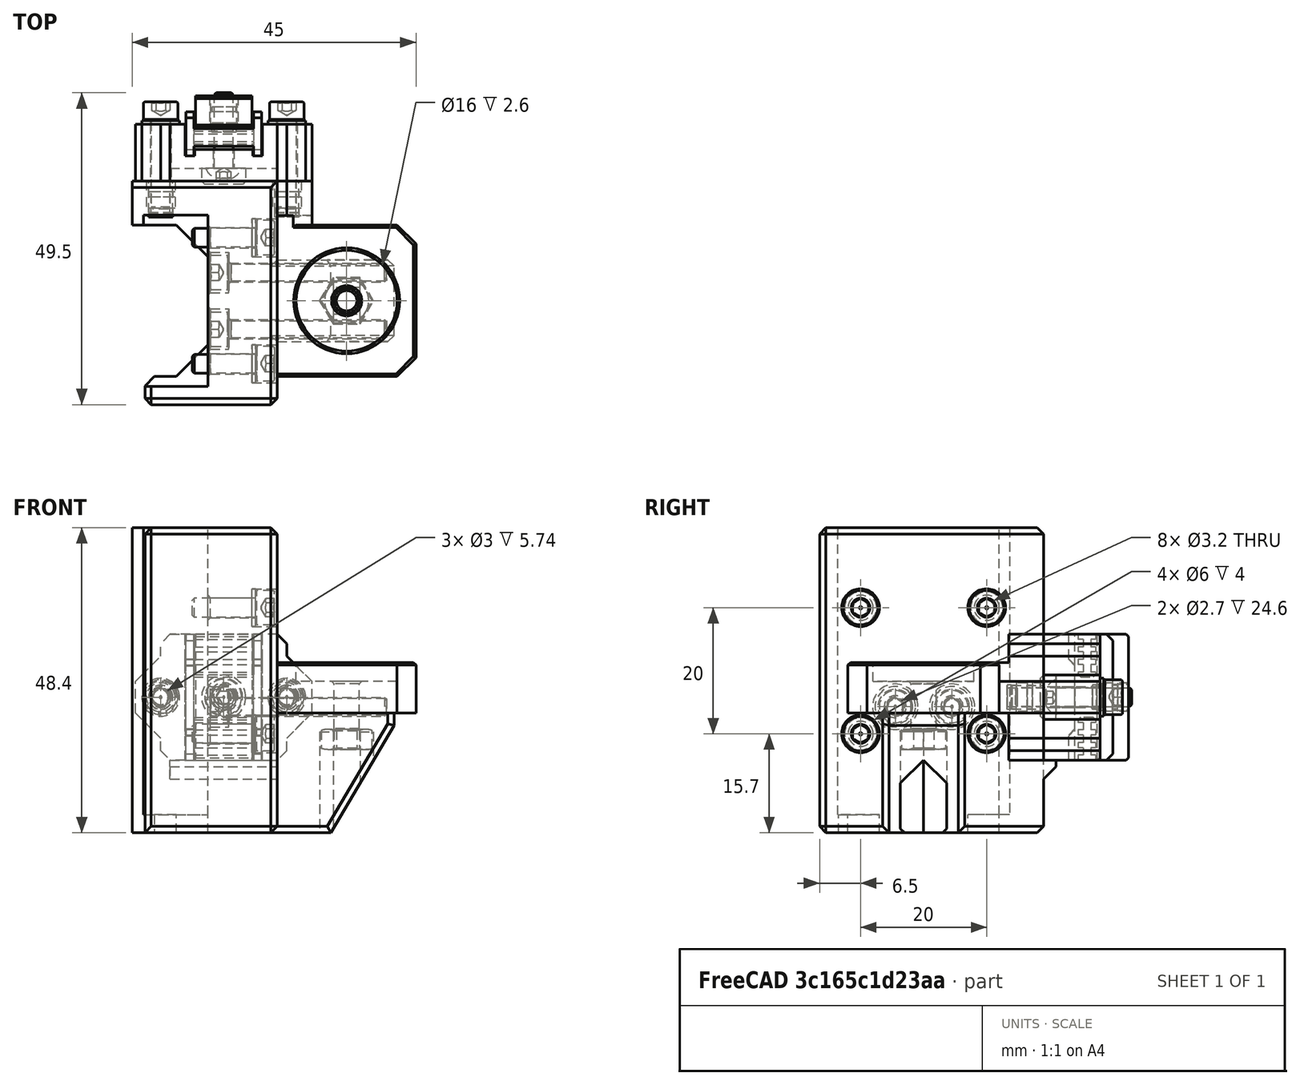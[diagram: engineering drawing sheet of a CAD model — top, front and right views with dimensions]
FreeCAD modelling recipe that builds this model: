
FCSTD DOCUMENT  (FreeCAD 0.19R24291 (Git))
Label: z-block-mount-left-assembly
License: Other
LicenseURL: GPL3
objects: Part::FeaturePython×19, Part::Feature×4, PartDesign::CoordinateSystem×1, App::Part×1
note: 24 computed .brp shape members not serialized (recipe doc carries the construction recipe); baked Part::Feature solids carry a one-line shape summary decoded from their .brp

FEATURE [Part::Feature] Cut002001001  label="z-belt-mounter-clamp-nut"
  Placement = pos=(2.5,36,18.5) rot=(-1,0,0;1.5708rad)
  shape: bbox 9 x 5 x 20 mm, 11 faces (baked)
FEATURE [Part::Feature] Chamfer004013007011015006002001  label="z-belt-block-mount"
  Placement = pos=(0,-12.5,0) rot=(0,0,1;0rad)
  shape: bbox 28 x 9 x 20 mm, 47 faces (baked)
FEATURE [Part::Feature] Cut028006004005011004003001010002002004006  label="z-belt-mounter-middle"
  Placement = pos=(0,-14,0) rot=(0,0,1;0rad)
  shape: bbox 12 x 7 x 20 mm, 80 faces (baked)
FEATURE [Part::FeaturePython] Washer  label="M3-Washer"  # Fasteners workbench fastener (typed FeaturePython)
  Placement = pos=(7,-10,32.7) rot=(0,1,0;1.5708rad)
  diameter = 4
  invert = false
  leftHanded = false
  matchOuter = true
  offset = 0
  type = 5
FEATURE [Part::FeaturePython] Washer001  label="M3-Washer008"  # Fasteners workbench fastener (typed FeaturePython)
  Placement = pos=(7,10,32.7) rot=(0,1,0;1.5708rad)
  diameter = 4
  invert = false
  leftHanded = false
  matchOuter = true
  offset = 0
  type = 5
FEATURE [Part::FeaturePython] Washer002  label="M3-Washer009"  # Fasteners workbench fastener (typed FeaturePython)
  Placement = pos=(7,-10,12.7) rot=(0,1,0;1.5708rad)
  diameter = 4
  invert = false
  leftHanded = false
  matchOuter = true
  offset = 0
  type = 5
FEATURE [Part::FeaturePython] Washer003  label="M3-Washer010"  # Fasteners workbench fastener (typed FeaturePython)
  Placement = pos=(7,10,12.7) rot=(0,1,0;1.5708rad)
  diameter = 4
  invert = false
  leftHanded = false
  matchOuter = true
  offset = 0
  type = 5
FEATURE [Part::FeaturePython] Screw  label="M3x10-Screw"  # Fasteners workbench fastener (typed FeaturePython)
  Placement = pos=(7.55,-10,32.7) rot=(0,1,0;1.5708rad)
  baseObject = -> Washer [Edge1]
  diameter = 4
  invert = false
  leftHanded = false
  length = 3
  lengthCustom = 10
  matchOuter = true
  offset = 0
  thread = false
  type = 34
FEATURE [Part::FeaturePython] Screw001  label="M3x10-Screw005"  # Fasteners workbench fastener (typed FeaturePython)
  Placement = pos=(7.55,10,32.7) rot=(0,1,0;1.5708rad)
  baseObject = -> Washer001 [Edge1]
  diameter = 4
  invert = false
  leftHanded = false
  length = 3
  lengthCustom = 10
  matchOuter = true
  offset = 0
  thread = false
  type = 34
FEATURE [Part::FeaturePython] Screw002  label="M3x10-Screw004"  # Fasteners workbench fastener (typed FeaturePython)
  Placement = pos=(7.55,-10,12.7) rot=(0,1,0;1.5708rad)
  baseObject = -> Washer002 [Edge1]
  diameter = 4
  invert = false
  leftHanded = false
  length = 3
  lengthCustom = 10
  matchOuter = true
  offset = 0
  thread = false
  type = 34
FEATURE [Part::FeaturePython] Screw003  label="M3x10-Screw003"  # Fasteners workbench fastener (typed FeaturePython)
  Placement = pos=(7.55,10,12.7) rot=(0,1,0;1.5708rad)
  baseObject = -> Washer003 [Edge1]
  diameter = 4
  invert = false
  leftHanded = false
  length = 3
  lengthCustom = 10
  matchOuter = true
  offset = 0
  thread = false
  type = 34
FEATURE [Part::FeaturePython] HeatSet  label="M3x4-HeatSet"  # WARN: FeaturePython — macro-defined, semantics opaque (R4)
  Placement = pos=(12.5,19,18.5) rot=(-1,0,0;1.5708rad)
  diameter = 2
  invert = false
  leftHanded = false
  offset = 0
FEATURE [Part::FeaturePython] HeatSet001  label="M3x4-HeatSet001"  # WARN: FeaturePython — macro-defined, semantics opaque (R4)
  Placement = pos=(-7.5,19,18.5) rot=(-1,0,0;1.5708rad)
  diameter = 2
  invert = false
  leftHanded = false
  offset = 0
FEATURE [Part::FeaturePython] HeatSet002  label="M3x4-HeatSet002"  # WARN: FeaturePython — macro-defined, semantics opaque (R4)
  Placement = pos=(2.5,32.5,18.5) rot=(-1,0,0;1.5708rad)
  baseObject = -> Cut002001001 [Edge21]
  diameter = 2
  invert = false
  leftHanded = false
  offset = 0
FEATURE [Part::FeaturePython] Washer004  label="M3-Washer006"  # Fasteners workbench fastener (typed FeaturePython)
  Placement = pos=(12.5,28,18.5) rot=(-1,0,0;1.5708rad)
  baseObject = -> Chamfer004013007011015006002001 [Edge96]
  diameter = 4
  invert = true
  leftHanded = false
  matchOuter = true
  offset = 0
  type = 5
FEATURE [Part::FeaturePython] Washer005  label="M3-Washer007"  # Fasteners workbench fastener (typed FeaturePython)
  Placement = pos=(-7.5,28,18.5) rot=(-1,0,0;1.5708rad)
  baseObject = -> Chamfer004013007011015006002001 [Edge15]
  diameter = 4
  invert = true
  leftHanded = false
  matchOuter = true
  offset = 0
  type = 5
FEATURE [Part::FeaturePython] Screw006  label="M3x14-Screw"  # Fasteners workbench fastener (typed FeaturePython)
  Placement = pos=(12.5,28.55,18.5) rot=(-1,0,0;1.5708rad)
  baseObject = -> Washer004 [Edge1]
  diameter = 4
  invert = false
  leftHanded = false
  length = 5
  lengthCustom = 14
  matchOuter = true
  offset = 0
  thread = false
  type = 34
FEATURE [Part::FeaturePython] Screw007  label="M3x14-Screw001"  # Fasteners workbench fastener (typed FeaturePython)
  Placement = pos=(-7.5,28.55,18.5) rot=(-1,0,0;1.5708rad)
  baseObject = -> Washer005 [Edge1]
  diameter = 4
  invert = false
  leftHanded = false
  length = 5
  lengthCustom = 14
  matchOuter = true
  offset = 0
  thread = false
  type = 34
FEATURE [Part::FeaturePython] Screw008  label="M3x12-Screw"  # Fasteners workbench fastener (typed FeaturePython)
  Placement = pos=(2.5,21,18.5) rot=(1,0,0;1.5708rad)
  baseObject = -> Chamfer004013007011015006002001 [Edge132]
  diameter = 1
  invert = false
  leftHanded = false
  length = 3
  lengthCustom = 12
  matchOuter = true
  offset = 0
  thread = false
  type = 40
FEATURE [PartDesign::CoordinateSystem] LCS_z_rail_block_mount_y_slider_1  label="LCS_z-rail-block-mount-y-slider"
  AttacherType = Attacher::AttachEngine3D
FEATURE [Part::Feature] Chamfer004013007011015006009007001005003063003001002001002001007002010001  label="z-rail-block-mount-left"
  shape: bbox 45 x 37.5 x 48.4 mm, 126 faces (baked)
FEATURE [Part::FeaturePython] Screw009  label="M3x25-Screw"  # Fasteners workbench fastener (typed FeaturePython)
  Placement = pos=(3.3,4.5,17) rot=(0,-1,0;1.5708rad)
  baseObject = -> Chamfer004013007011015006009007001005003063003001002001002001007002010001 [Edge284]
  diameter = 4
  invert = true
  leftHanded = false
  length = 8
  lengthCustom = 25
  matchOuter = true
  offset = 0
  thread = false
  type = 36
FEATURE [Part::FeaturePython] Screw010  label="M3x25-Screw001"  # Fasteners workbench fastener (typed FeaturePython)
  Placement = pos=(3.3,-4.5,17) rot=(0,-1,0;1.5708rad)
  baseObject = -> Chamfer004013007011015006009007001005003063003001002001002001007002010001 [Edge285]
  diameter = 4
  invert = true
  leftHanded = false
  length = 8
  lengthCustom = 25
  matchOuter = true
  offset = 0
  thread = false
  type = 36
FEATURE [Part::FeaturePython] Nut  label="M4-Nut"  # Fasteners workbench fastener (typed FeaturePython)
  Placement = pos=(22,0,13.4) rot=(-1,0,0;3.14159rad)
  baseObject = -> Chamfer004013007011015006009007001005003063003001002001002001007002010001 [Edge1]
  diameter = 6
  invert = true
  leftHanded = false
  matchOuter = true
  offset = 0
  thread = false
  type = 9
FEATURE [App::Part] Part  label="z-rail-block-mount-y-slider"
  Group = -> [Cut002001001,Chamfer004013007011015006002001,Cut028006004005011004003001010002002004006,Washer,Washer001,Washer002,Washer003,Screw003,Screw002,Screw001,Screw,HeatSet,HeatSet001,HeatSet002,Washer004,Washer005,Screw006,Screw007,Screw008,LCS_z_rail_block_mount_y_slider_1,Chamfer004013007011015006009007001005003063003001002001002001007002010001,Screw009,Screw010,Nut]
  Origin = -> Origin
